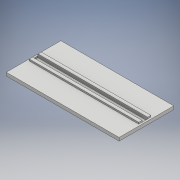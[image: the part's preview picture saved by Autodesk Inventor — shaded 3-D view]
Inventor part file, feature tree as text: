
AUTODESK INVENTOR PART (.ipt)
format: ipt  version: 2018.3 (Build 223284000, 284)  size: 134,656 bytes
history: native  units: mm
features: extrude x4, sketch x4
ambient origin geometry x8: Origin, YZ Plane, XZ Plane, XY Plane, X Axis, Y Axis, Z Axis, Center Point
bodies: Solid1 (feature_tree)
feature tree (8):
  extrude  "Extrusion1"  Depth=34.5mm
  extrude  "Extrusion2"  Depth=34.5mm
  extrude  "Extrusion3"  Depth=7.5mm
  extrude  "Extrusion4"  Depth=0.5mm
  sketch  "Sketch1"  dims[d0=16.7mm d1=34.5mm]
  sketch  "Sketch2"  dims[d2=1.0mm d3=0.0mm d4=34.5mm]
  sketch  "Sketch3"  dims[d5=1.7mm d6=7.5mm]
  sketch  "Sketch4"  dims[d7=0.5mm d8=0.0mm d9=0.5mm d10=0.5mm d11=0.5mm d12=0.0mm d13=1.0mm d14=1.0mm d15=0.5mm d16=0.0mm]
